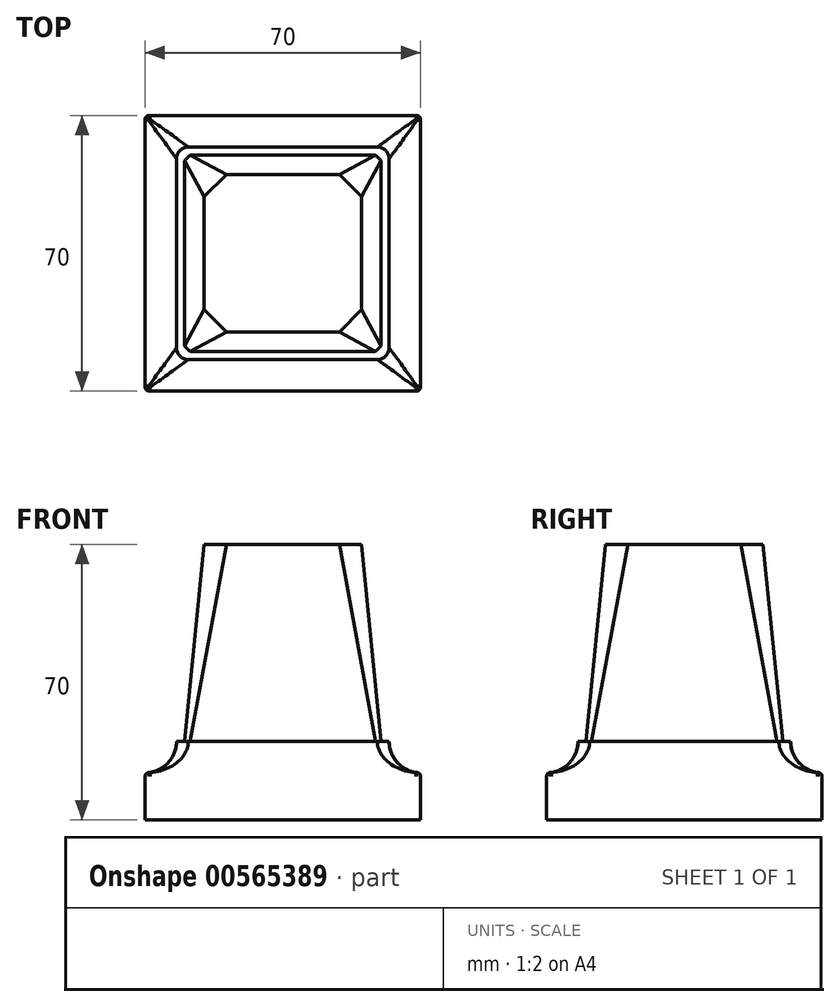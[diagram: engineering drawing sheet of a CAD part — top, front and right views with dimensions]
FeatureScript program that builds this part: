
annotation { "Feature Type Name" : "Feature", "Feature Type Description" : "" }
export const myFeature = defineFeature(function(context is Context, id is Id, definition is map)
    precondition{}
    {
        {
            var Q0;
            Q0=qCreatedBy(makeId("Top.planeOp"),FACE);
            var sketch = newSketch(context, id + "F0", { "sketchPlane" : qUnion([Q0])});
            skLineSegment(sketch, "E0.bottom", {"start": v(-35.62, 33.53) * mm, "end": v(34.38, 33.53) * mm});
            skLineSegment(sketch, "E0.top", {"start": v(-35.62, -36.47) * mm, "end": v(34.38, -36.47) * mm});
            skLineSegment(sketch, "E0.left", {"start": v(-35.62, 33.53) * mm, "end": v(-35.62, -36.47) * mm});
            skLineSegment(sketch, "E0.right", {"start": v(34.38, 33.53) * mm, "end": v(34.38, -36.47) * mm});
            skSolve(sketch);
        }
        {
            var Q0;
            Q0 = qSketchRegion(id + "F0", true);
            extrude(context, id + "F1", {"entities" : qUnion([Q0]), "depth" : 20 * mm, "offsetDistance" : 25 * mm});
        }
        {
            var Q0;
            Q0=makeQuery(id+"F1.opExtrude","SWEPT_FACE",FACE,{"disambiguationData":[OSD([sQuery(id+"F0.wireOp",EDGE,"E0.top")])]});
            var sketch = newSketch(context, id + "F2", { "sketchPlane" : qUnion([Q0])});
            skCircle(sketch, "E1", {"center": v(34.38, 20) * mm, "radius": 8 * mm});
            skCircle(sketch, "E2", {"center": v(-35.62, 20) * mm, "radius": 8 * mm});
            skSolve(sketch);
        }
        {
            var Q0;
            Q0=makeQuery(id+"F1.opExtrude","SWEPT_FACE",FACE,{"disambiguationData":[OSD([sQuery(id+"F0.wireOp",EDGE,"E0.right")])]});
            var sketch = newSketch(context, id + "F3", { "sketchPlane" : qUnion([Q0])});
            skCircle(sketch, "E3", {"center": v(33.53, 20) * mm, "radius": 8 * mm});
            skCircle(sketch, "E4", {"center": v(-36.47, 20) * mm, "radius": 8 * mm});
            skSolve(sketch);
        }
        {
            var Q0;
            Q0 = qSketchRegion(id + "F2", true);
            var Q1;
            Q1=makeQuery(id+"F1.opExtrude","SWEPT_FACE",FACE,{"disambiguationData":[OSD([sQuery(id+"F0.wireOp",EDGE,"E0.bottom")])]});
            extrude(context, id + "F4", {"entities" : qUnion([Q0]), "operationType" : NewBodyOperationType.REMOVE, "endBound" : BoundingType.UP_TO_SURFACE, "oppositeDirection" : true, "depth" : 25 * mm, "endBoundEntityFace" : qUnion([Q1]), "offsetDistance" : 25 * mm});
        }
        {
            var Q0;
            Q0 = qSketchRegion(id + "F3", true);
            var Q1;
            Q1=makeQuery(id+"F1.opExtrude","SWEPT_FACE",FACE,{"disambiguationData":[OSD([sQuery(id+"F0.wireOp",EDGE,"E0.left")])]});
            extrude(context, id + "F5", {"entities" : qUnion([Q0]), "operationType" : NewBodyOperationType.REMOVE, "endBound" : BoundingType.UP_TO_SURFACE, "oppositeDirection" : true, "depth" : 25 * mm, "endBoundEntityFace" : qUnion([Q1]), "offsetDistance" : 25 * mm});
        }
        {
            var Q0;
            Q0=makeQuery(id+"F1.opExtrude","CAP_FACE",FACE,{"disambiguationData":[OSD([sQuery(id+"F0.wireOp",EDGE,"E0.bottom"),sQuery(id+"F0.wireOp",EDGE,"E0.top"),sQuery(id+"F0.wireOp",EDGE,"E0.left"),sQuery(id+"F0.wireOp",EDGE,"E0.right")])],"isStart":false});
            var sketch = newSketch(context, id + "F6", { "sketchPlane" : qUnion([Q0])});
            skLineSegment(sketch, "E5", {"start": v(-25.62, 22.12) * mm, "end": v(-24.2, 23.53) * mm});
            skLineSegment(sketch, "E6", {"start": v(-24.2, 23.53) * mm, "end": v(22.97, 23.53) * mm});
            skLineSegment(sketch, "E7", {"start": v(22.97, 23.53) * mm, "end": v(24.38, 22.12) * mm});
            skLineSegment(sketch, "E8", {"start": v(24.38, 22.12) * mm, "end": v(24.38, -25.06) * mm});
            skLineSegment(sketch, "E9", {"start": v(24.38, -25.06) * mm, "end": v(22.97, -26.47) * mm});
            skLineSegment(sketch, "E10", {"start": v(22.97, -26.47) * mm, "end": v(-24.2, -26.47) * mm});
            skLineSegment(sketch, "E11", {"start": v(-24.2, -26.47) * mm, "end": v(-25.62, -25.06) * mm});
            skLineSegment(sketch, "E12", {"start": v(-25.62, -25.06) * mm, "end": v(-25.62, 22.12) * mm});
            skSolve(sketch);
        }
        {
            var Q0;
            Q0=makeQuery(id+"F5.boolean.opBoolean","INTERSECT",EDGE,{"derivedFrom":[makeQuery(id+"F4.boolean.opBoolean","COPY",FACE,{"derivedFrom":makeQuery(id+"F4.opExtrude","SWEPT_FACE",FACE,{"disambiguationData":[OSD([sQuery(id+"F2.wireOp",EDGE,"E2")])]})}),makeQuery(id+"F5.opExtrude","SWEPT_FACE",FACE,{"disambiguationData":[OSD([sQuery(id+"F3.wireOp",EDGE,"E3")])]})]});
            var Q1;
            Q1=makeQuery(id+"F5.boolean.opBoolean","INTERSECT",EDGE,{"derivedFrom":[makeQuery(id+"F4.boolean.opBoolean","COPY",FACE,{"derivedFrom":makeQuery(id+"F4.opExtrude","SWEPT_FACE",FACE,{"disambiguationData":[OSD([sQuery(id+"F2.wireOp",EDGE,"E2")])]})}),makeQuery(id+"F5.opExtrude","SWEPT_FACE",FACE,{"disambiguationData":[OSD([sQuery(id+"F3.wireOp",EDGE,"E4")])]})]});
            var Q2;
            Q2=makeQuery(id+"F5.boolean.opBoolean","INTERSECT",EDGE,{"derivedFrom":[makeQuery(id+"F4.boolean.opBoolean","COPY",FACE,{"derivedFrom":makeQuery(id+"F4.opExtrude","SWEPT_FACE",FACE,{"disambiguationData":[OSD([sQuery(id+"F2.wireOp",EDGE,"E1")])]})}),makeQuery(id+"F5.opExtrude","SWEPT_FACE",FACE,{"disambiguationData":[OSD([sQuery(id+"F3.wireOp",EDGE,"E4")])]})]});
            var Q3;
            Q3=makeQuery(id+"F5.boolean.opBoolean","INTERSECT",EDGE,{"derivedFrom":[makeQuery(id+"F4.boolean.opBoolean","COPY",FACE,{"derivedFrom":makeQuery(id+"F4.opExtrude","SWEPT_FACE",FACE,{"disambiguationData":[OSD([sQuery(id+"F2.wireOp",EDGE,"E1")])]})}),makeQuery(id+"F5.opExtrude","SWEPT_FACE",FACE,{"disambiguationData":[OSD([sQuery(id+"F3.wireOp",EDGE,"E3")])]})]});
            fillet(context, id + "F7", {"entities" : qUnion([Q0, Q1, Q2, Q3]), "radius" : 3 * mm, "tangentPropagation" : true, "allowEdgeOverflow" : false});
        }
        {
            var Q0;
            Q0=makeQuery(id+"F1.opExtrude","CAP_FACE",FACE,{"disambiguationData":[OSD([sQuery(id+"F0.wireOp",EDGE,"E0.bottom"),sQuery(id+"F0.wireOp",EDGE,"E0.top"),sQuery(id+"F0.wireOp",EDGE,"E0.left"),sQuery(id+"F0.wireOp",EDGE,"E0.right")])],"isStart":false});
            cPlane(context, id + "F8", {"entities" : qUnion([Q0]), "cplaneType" : CPlaneType.OFFSET, "offset" : 50 * mm, "width" : 150 * mm, "height" : 150 * mm});
        }
        {
            var Q0;
            Q0=qCreatedBy(id+"F8.planeOp",FACE);
            var sketch = newSketch(context, id + "F9", { "sketchPlane" : qUnion([Q0])});
            skLineSegment(sketch, "E13", {"start": v(-20.62, 12.87) * mm, "end": v(-14.96, 18.53) * mm});
            skLineSegment(sketch, "E14", {"start": v(-14.96, 18.53) * mm, "end": v(13.73, 18.53) * mm});
            skLineSegment(sketch, "E15", {"start": v(13.73, 18.53) * mm, "end": v(19.38, 12.87) * mm});
            skLineSegment(sketch, "E16", {"start": v(19.38, 12.87) * mm, "end": v(19.38, -15.81) * mm});
            skLineSegment(sketch, "E17", {"start": v(19.38, -15.81) * mm, "end": v(13.73, -21.47) * mm});
            skLineSegment(sketch, "E18", {"start": v(13.73, -21.47) * mm, "end": v(-14.96, -21.47) * mm});
            skLineSegment(sketch, "E19", {"start": v(-14.96, -21.47) * mm, "end": v(-20.62, -15.81) * mm});
            skLineSegment(sketch, "E20", {"start": v(-20.62, -15.81) * mm, "end": v(-20.62, 12.87) * mm});
            skSolve(sketch);
        }
        {
            var Q1;
            Q1=makeQuery(id+"F6.imprint","IMPRINT",FACE,{"disambiguationData":[TD([[makeQuery(id+"F6.imprint","IMPRINT",EDGE,{"derivedFrom":sQuery(id+"F6.wireOp",EDGE,"E5")}),-1.0]])]});
            var Q2;
            Q2=makeQuery(id+"F9.imprint","IMPRINT",FACE,{"disambiguationData":[TD([[makeQuery(id+"F9.imprint","IMPRINT",EDGE,{"derivedFrom":sQuery(id+"F9.wireOp",EDGE,"E13")}),-1.0]])]});
            loft(context, id + "F10", {"operationType" : NewBodyOperationType.ADD, "sheetProfilesArray" : [{ "sheetProfileEntities" : qUnion([Q1]) }, { "sheetProfileEntities" : qUnion([Q2]) }]});
        }
        {
            var Q0;
            Q0=makeQuery(id+"F1.opExtrude","SWEPT_EDGE",EDGE,{"disambiguationData":[OSD([sQuery(id+"F0.wireOp",EDGE,"E0.top"),sQuery(id+"F0.wireOp",EDGE,"E0.right")])]});
            var Q1;
            Q1=makeQuery(id+"F1.opExtrude","SWEPT_EDGE",EDGE,{"disambiguationData":[OSD([sQuery(id+"F0.wireOp",EDGE,"E0.top"),sQuery(id+"F0.wireOp",EDGE,"E0.left")])]});
            var Q2;
            Q2=makeQuery(id+"F1.opExtrude","SWEPT_EDGE",EDGE,{"disambiguationData":[OSD([sQuery(id+"F0.wireOp",EDGE,"E0.bottom"),sQuery(id+"F0.wireOp",EDGE,"E0.right")])]});
            var Q3;
            Q3=makeQuery(id+"F1.opExtrude","SWEPT_EDGE",EDGE,{"disambiguationData":[OSD([sQuery(id+"F0.wireOp",EDGE,"E0.bottom"),sQuery(id+"F0.wireOp",EDGE,"E0.left")])]});
            fillet(context, id + "F11", {"entities" : qUnion([Q0, Q1, Q2, Q3]), "radius" : 1 * mm, "tangentPropagation" : true, "allowEdgeOverflow" : false});
        }
        {
            var Q0;
            Q0=makeQuery(id+"F4.boolean.opBoolean","INTERSECT",EDGE,{"derivedFrom":[makeQuery(id+"F1.opExtrude","SWEPT_FACE",FACE,{"disambiguationData":[OSD([sQuery(id+"F0.wireOp",EDGE,"E0.left")])]}),makeQuery(id+"F4.opExtrude","SWEPT_FACE",FACE,{"disambiguationData":[OSD([sQuery(id+"F2.wireOp",EDGE,"E2")])]})]});
            var Q1;
            Q1=makeQuery(id+"F11.opFillet","BLEND_EDGE",EDGE,{"blendedFrom":[makeQuery(id+"F1.opExtrude","SWEPT_EDGE",EDGE,{"disambiguationData":[OSD([sQuery(id+"F0.wireOp",EDGE,"E0.top"),sQuery(id+"F0.wireOp",EDGE,"E0.left")])]}),makeQuery(id+"F4.boolean.opBoolean","COPY",FACE,{"derivedFrom":makeQuery(id+"F4.opExtrude","SWEPT_FACE",FACE,{"disambiguationData":[OSD([sQuery(id+"F2.wireOp",EDGE,"E2")])]})})],"blendedInto":[makeQuery(id+"F4.boolean.opBoolean","COPY",FACE,{"derivedFrom":makeQuery(id+"F4.opExtrude","SWEPT_FACE",FACE,{"disambiguationData":[OSD([sQuery(id+"F2.wireOp",EDGE,"E2")])]})})]});
            var Q2;
            Q2=makeQuery(id+"F11.opFillet","BLEND_EDGE",EDGE,{"blendedFrom":[makeQuery(id+"F1.opExtrude","SWEPT_EDGE",EDGE,{"disambiguationData":[OSD([sQuery(id+"F0.wireOp",EDGE,"E0.top"),sQuery(id+"F0.wireOp",EDGE,"E0.left")])]}),makeQuery(id+"F5.boolean.opBoolean","COPY",FACE,{"derivedFrom":makeQuery(id+"F5.opExtrude","SWEPT_FACE",FACE,{"disambiguationData":[OSD([sQuery(id+"F3.wireOp",EDGE,"E4")])]})})],"blendedInto":[makeQuery(id+"F5.boolean.opBoolean","COPY",FACE,{"derivedFrom":makeQuery(id+"F5.opExtrude","SWEPT_FACE",FACE,{"disambiguationData":[OSD([sQuery(id+"F3.wireOp",EDGE,"E4")])]})})]});
            var Q3;
            Q3=makeQuery(id+"F11.opFillet","BLEND_EDGE",EDGE,{"blendedFrom":[makeQuery(id+"F1.opExtrude","SWEPT_EDGE",EDGE,{"disambiguationData":[OSD([sQuery(id+"F0.wireOp",EDGE,"E0.top"),sQuery(id+"F0.wireOp",EDGE,"E0.left")])]}),makeQuery(id+"F7.opFillet","BLEND_FACE",FACE,{"disambiguationData":[OSD([sQuery(id+"F2.wireOp",EDGE,"E2"),sQuery(id+"F3.wireOp",EDGE,"E4")])]})],"blendedInto":[makeQuery(id+"F7.opFillet","BLEND_FACE",FACE,{"disambiguationData":[OSD([sQuery(id+"F2.wireOp",EDGE,"E2"),sQuery(id+"F3.wireOp",EDGE,"E4")])]})]});
            var Q4;
            Q4=makeQuery(id+"F5.boolean.opBoolean","INTERSECT",EDGE,{"derivedFrom":[makeQuery(id+"F1.opExtrude","SWEPT_FACE",FACE,{"disambiguationData":[OSD([sQuery(id+"F0.wireOp",EDGE,"E0.top")])]}),makeQuery(id+"F5.opExtrude","SWEPT_FACE",FACE,{"disambiguationData":[OSD([sQuery(id+"F3.wireOp",EDGE,"E4")])]})]});
            var Q5;
            Q5=makeQuery(id+"F11.opFillet","BLEND_EDGE",EDGE,{"blendedFrom":[makeQuery(id+"F1.opExtrude","SWEPT_EDGE",EDGE,{"disambiguationData":[OSD([sQuery(id+"F0.wireOp",EDGE,"E0.top"),sQuery(id+"F0.wireOp",EDGE,"E0.right")])]}),makeQuery(id+"F5.boolean.opBoolean","COPY",FACE,{"derivedFrom":makeQuery(id+"F5.opExtrude","SWEPT_FACE",FACE,{"disambiguationData":[OSD([sQuery(id+"F3.wireOp",EDGE,"E4")])]})})],"blendedInto":[makeQuery(id+"F5.boolean.opBoolean","COPY",FACE,{"derivedFrom":makeQuery(id+"F5.opExtrude","SWEPT_FACE",FACE,{"disambiguationData":[OSD([sQuery(id+"F3.wireOp",EDGE,"E4")])]})})]});
            var Q6;
            Q6=makeQuery(id+"F11.opFillet","BLEND_EDGE",EDGE,{"blendedFrom":[makeQuery(id+"F1.opExtrude","SWEPT_EDGE",EDGE,{"disambiguationData":[OSD([sQuery(id+"F0.wireOp",EDGE,"E0.top"),sQuery(id+"F0.wireOp",EDGE,"E0.right")])]}),makeQuery(id+"F7.opFillet","BLEND_FACE",FACE,{"disambiguationData":[OSD([sQuery(id+"F2.wireOp",EDGE,"E1"),sQuery(id+"F3.wireOp",EDGE,"E4")])]})],"blendedInto":[makeQuery(id+"F7.opFillet","BLEND_FACE",FACE,{"disambiguationData":[OSD([sQuery(id+"F2.wireOp",EDGE,"E1"),sQuery(id+"F3.wireOp",EDGE,"E4")])]})]});
            var Q7;
            Q7=makeQuery(id+"F11.opFillet","BLEND_EDGE",EDGE,{"blendedFrom":[makeQuery(id+"F1.opExtrude","SWEPT_EDGE",EDGE,{"disambiguationData":[OSD([sQuery(id+"F0.wireOp",EDGE,"E0.top"),sQuery(id+"F0.wireOp",EDGE,"E0.right")])]}),makeQuery(id+"F4.boolean.opBoolean","COPY",FACE,{"derivedFrom":makeQuery(id+"F4.opExtrude","SWEPT_FACE",FACE,{"disambiguationData":[OSD([sQuery(id+"F2.wireOp",EDGE,"E1")])]})})],"blendedInto":[makeQuery(id+"F4.boolean.opBoolean","COPY",FACE,{"derivedFrom":makeQuery(id+"F4.opExtrude","SWEPT_FACE",FACE,{"disambiguationData":[OSD([sQuery(id+"F2.wireOp",EDGE,"E1")])]})})]});
            var Q8;
            Q8=makeQuery(id+"F4.boolean.opBoolean","INTERSECT",EDGE,{"derivedFrom":[makeQuery(id+"F1.opExtrude","SWEPT_FACE",FACE,{"disambiguationData":[OSD([sQuery(id+"F0.wireOp",EDGE,"E0.right")])]}),makeQuery(id+"F4.opExtrude","SWEPT_FACE",FACE,{"disambiguationData":[OSD([sQuery(id+"F2.wireOp",EDGE,"E1")])]})]});
            var Q9;
            Q9=makeQuery(id+"F11.opFillet","BLEND_EDGE",EDGE,{"blendedFrom":[makeQuery(id+"F1.opExtrude","SWEPT_EDGE",EDGE,{"disambiguationData":[OSD([sQuery(id+"F0.wireOp",EDGE,"E0.bottom"),sQuery(id+"F0.wireOp",EDGE,"E0.right")])]}),makeQuery(id+"F4.boolean.opBoolean","COPY",FACE,{"derivedFrom":makeQuery(id+"F4.opExtrude","SWEPT_FACE",FACE,{"disambiguationData":[OSD([sQuery(id+"F2.wireOp",EDGE,"E1")])]})})],"blendedInto":[makeQuery(id+"F4.boolean.opBoolean","COPY",FACE,{"derivedFrom":makeQuery(id+"F4.opExtrude","SWEPT_FACE",FACE,{"disambiguationData":[OSD([sQuery(id+"F2.wireOp",EDGE,"E1")])]})})]});
            var Q10;
            Q10=makeQuery(id+"F11.opFillet","BLEND_EDGE",EDGE,{"blendedFrom":[makeQuery(id+"F1.opExtrude","SWEPT_EDGE",EDGE,{"disambiguationData":[OSD([sQuery(id+"F0.wireOp",EDGE,"E0.bottom"),sQuery(id+"F0.wireOp",EDGE,"E0.right")])]}),makeQuery(id+"F7.opFillet","BLEND_FACE",FACE,{"disambiguationData":[OSD([sQuery(id+"F2.wireOp",EDGE,"E1"),sQuery(id+"F3.wireOp",EDGE,"E3")])]})],"blendedInto":[makeQuery(id+"F7.opFillet","BLEND_FACE",FACE,{"disambiguationData":[OSD([sQuery(id+"F2.wireOp",EDGE,"E1"),sQuery(id+"F3.wireOp",EDGE,"E3")])]})]});
            var Q11;
            Q11=makeQuery(id+"F11.opFillet","BLEND_EDGE",EDGE,{"blendedFrom":[makeQuery(id+"F1.opExtrude","SWEPT_EDGE",EDGE,{"disambiguationData":[OSD([sQuery(id+"F0.wireOp",EDGE,"E0.bottom"),sQuery(id+"F0.wireOp",EDGE,"E0.right")])]}),makeQuery(id+"F5.boolean.opBoolean","COPY",FACE,{"derivedFrom":makeQuery(id+"F5.opExtrude","SWEPT_FACE",FACE,{"disambiguationData":[OSD([sQuery(id+"F3.wireOp",EDGE,"E3")])]})})],"blendedInto":[makeQuery(id+"F5.boolean.opBoolean","COPY",FACE,{"derivedFrom":makeQuery(id+"F5.opExtrude","SWEPT_FACE",FACE,{"disambiguationData":[OSD([sQuery(id+"F3.wireOp",EDGE,"E3")])]})})]});
            var Q12;
            Q12=makeQuery(id+"F5.boolean.opBoolean","INTERSECT",EDGE,{"derivedFrom":[makeQuery(id+"F1.opExtrude","SWEPT_FACE",FACE,{"disambiguationData":[OSD([sQuery(id+"F0.wireOp",EDGE,"E0.bottom")])]}),makeQuery(id+"F5.opExtrude","SWEPT_FACE",FACE,{"disambiguationData":[OSD([sQuery(id+"F3.wireOp",EDGE,"E3")])]})]});
            var Q13;
            Q13=makeQuery(id+"F11.opFillet","BLEND_EDGE",EDGE,{"blendedFrom":[makeQuery(id+"F1.opExtrude","SWEPT_EDGE",EDGE,{"disambiguationData":[OSD([sQuery(id+"F0.wireOp",EDGE,"E0.bottom"),sQuery(id+"F0.wireOp",EDGE,"E0.left")])]}),makeQuery(id+"F5.boolean.opBoolean","COPY",FACE,{"derivedFrom":makeQuery(id+"F5.opExtrude","SWEPT_FACE",FACE,{"disambiguationData":[OSD([sQuery(id+"F3.wireOp",EDGE,"E3")])]})})],"blendedInto":[makeQuery(id+"F5.boolean.opBoolean","COPY",FACE,{"derivedFrom":makeQuery(id+"F5.opExtrude","SWEPT_FACE",FACE,{"disambiguationData":[OSD([sQuery(id+"F3.wireOp",EDGE,"E3")])]})})]});
            var Q14;
            Q14=makeQuery(id+"F11.opFillet","BLEND_EDGE",EDGE,{"blendedFrom":[makeQuery(id+"F1.opExtrude","SWEPT_EDGE",EDGE,{"disambiguationData":[OSD([sQuery(id+"F0.wireOp",EDGE,"E0.bottom"),sQuery(id+"F0.wireOp",EDGE,"E0.left")])]}),makeQuery(id+"F7.opFillet","BLEND_FACE",FACE,{"disambiguationData":[OSD([sQuery(id+"F2.wireOp",EDGE,"E2"),sQuery(id+"F3.wireOp",EDGE,"E3")])]})],"blendedInto":[makeQuery(id+"F7.opFillet","BLEND_FACE",FACE,{"disambiguationData":[OSD([sQuery(id+"F2.wireOp",EDGE,"E2"),sQuery(id+"F3.wireOp",EDGE,"E3")])]})]});
            var Q15;
            Q15=makeQuery(id+"F11.opFillet","BLEND_EDGE",EDGE,{"blendedFrom":[makeQuery(id+"F1.opExtrude","SWEPT_EDGE",EDGE,{"disambiguationData":[OSD([sQuery(id+"F0.wireOp",EDGE,"E0.bottom"),sQuery(id+"F0.wireOp",EDGE,"E0.left")])]}),makeQuery(id+"F4.boolean.opBoolean","COPY",FACE,{"derivedFrom":makeQuery(id+"F4.opExtrude","SWEPT_FACE",FACE,{"disambiguationData":[OSD([sQuery(id+"F2.wireOp",EDGE,"E2")])]})})],"blendedInto":[makeQuery(id+"F4.boolean.opBoolean","COPY",FACE,{"derivedFrom":makeQuery(id+"F4.opExtrude","SWEPT_FACE",FACE,{"disambiguationData":[OSD([sQuery(id+"F2.wireOp",EDGE,"E2")])]})})]});
            fillet(context, id + "F12", {"entities" : qUnion([Q0, Q1, Q2, Q3, Q4, Q5, Q6, Q7, Q8, Q9, Q10, Q11, Q12, Q13, Q14, Q15]), "radius" : 1 * mm, "tangentPropagation" : true, "allowEdgeOverflow" : false});
        }
    });
